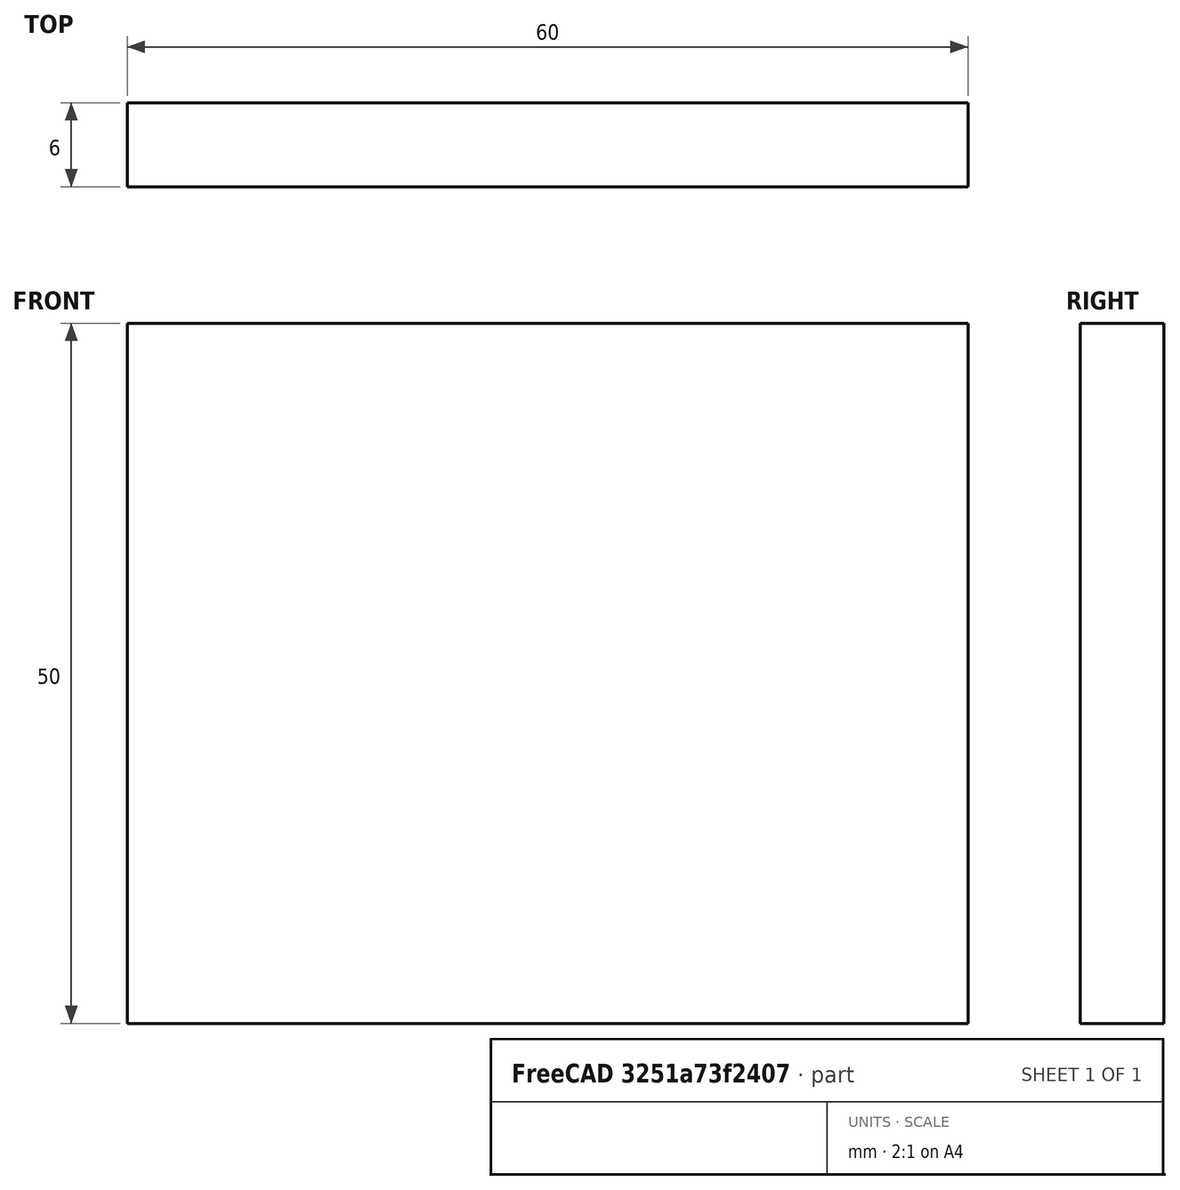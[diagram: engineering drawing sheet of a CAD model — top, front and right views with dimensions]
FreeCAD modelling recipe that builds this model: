
FCSTD DOCUMENT  (FreeCAD 0.15R4671 (Git))
Label: Flat Bar 60x6 EN10058 S235JR
License: All rights reserved
LicenseURL: http://en.wikipedia.org/wiki/All_rights_reserved
objects: Sketcher::SketchObject×1, Part::Extrusion×1
note: 2 computed .brp shape members not serialized (recipe doc carries the construction recipe); baked Part::Feature solids carry a one-line shape summary decoded from their .brp

FEATURE [Sketcher::SketchObject] Sketch
  sketch-geometry (4):
    g0: LineSegment StartX=-30 StartY=-3 StartZ=0 EndX=30 EndY=-3 EndZ=0
    g1: LineSegment StartX=30 StartY=-3 StartZ=0 EndX=30 EndY=3 EndZ=0
    g2: LineSegment StartX=30 StartY=3 StartZ=0 EndX=-30 EndY=3 EndZ=0
    g3: LineSegment StartX=-30 StartY=3 StartZ=0 EndX=-30 EndY=-3 EndZ=0
  constraints (12):
    c: Coincident(g0,g1)
    c: Coincident(g1,g2)
    c: Coincident(g2,g3)
    c: Coincident(g3,g0)
    c: Horizontal(g0)
    c: Horizontal(g2)
    c: Vertical(g1)
    c: Vertical(g3)
    c: Symmetric(g1,g2,g-2)
    c: Symmetric(g0,g1,g-1)
    c: DistanceY(g1) = 6
    c: DistanceX(g0) = 60
FEATURE [Part::Extrusion] Extrude  label="Flat Bar 60x6 EN10058 S235JR"
  Base = -> Sketch
  Dir = (0,0,50)
  Solid = true
